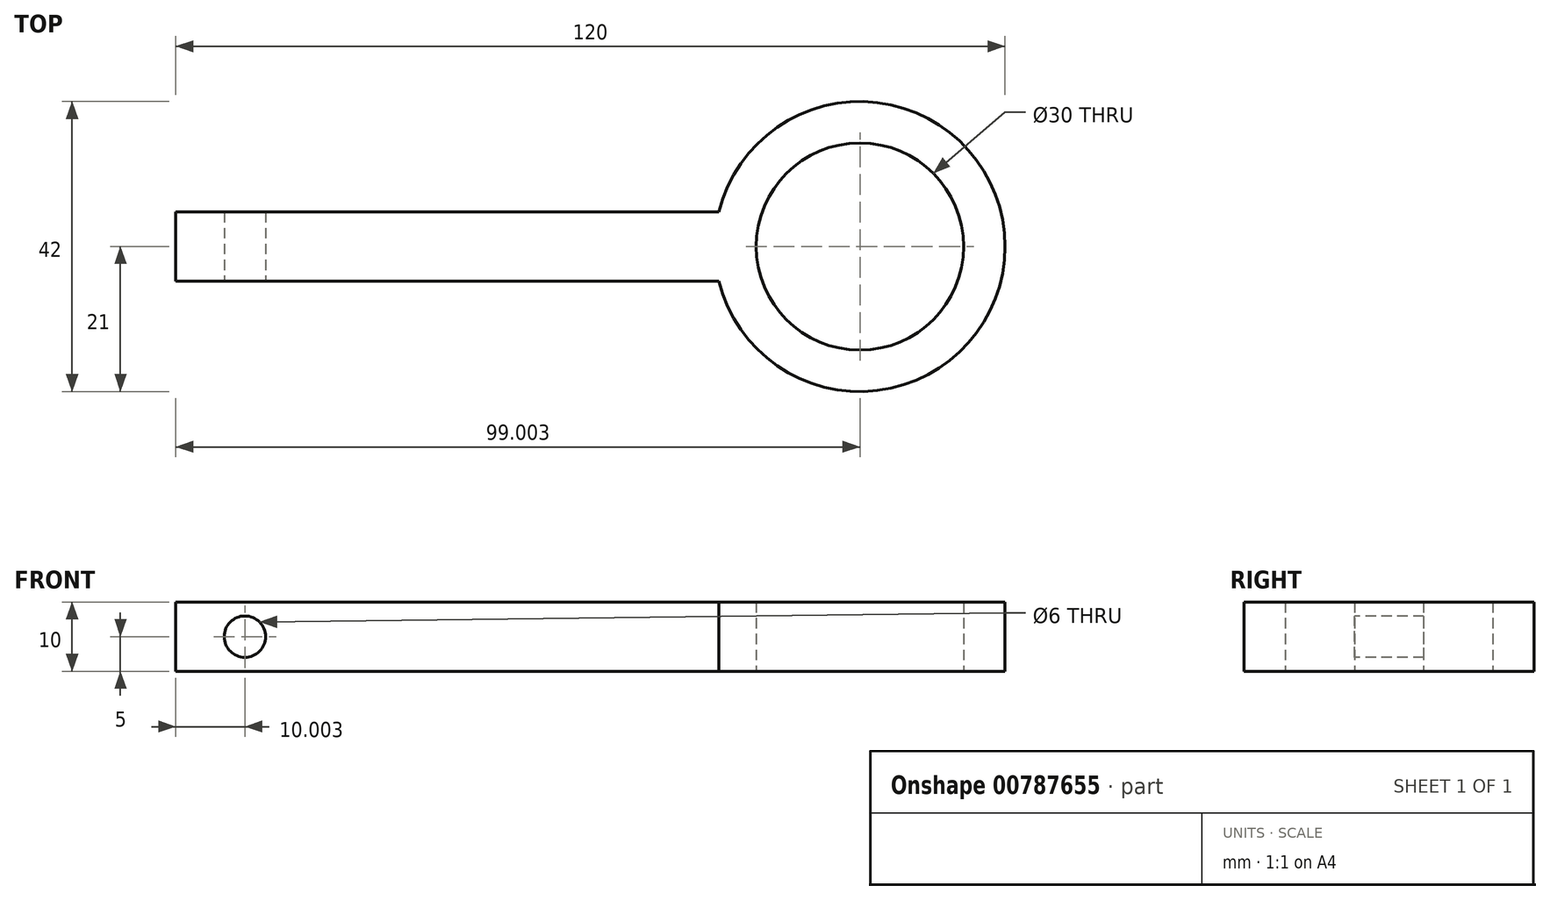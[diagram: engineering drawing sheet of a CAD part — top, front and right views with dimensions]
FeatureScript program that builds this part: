
annotation { "Feature Type Name" : "Feature", "Feature Type Description" : "" }
export const myFeature = defineFeature(function(context is Context, id is Id, definition is map)
    precondition{}
    {
        {
            var Q0;
            Q0=qCreatedBy(makeId("Top.planeOp"),FACE);
            var sketch = newSketch(context, id + "F0", { "sketchPlane" : qUnion([Q0])});
            skLineSegment(sketch, "E0.bottom", {"start": v(-74.3, 5) * mm, "end": v(4.3, 5) * mm});
            skLineSegment(sketch, "E0.top", {"start": v(-74.3, -5) * mm, "end": v(4.3, -5) * mm});
            skLineSegment(sketch, "E0.left", {"start": v(-74.3, 5) * mm, "end": v(-74.3, -5) * mm});
            skArc(sketch, "E1", {"start": v(4.3, -5) * mm, "mid": v(45.7, 0) * mm, "end": v(4.3, 5) * mm});
            skCircle(sketch, "E2", {"center": v(24.7, 0) * mm, "radius": 15 * mm});
            skPoint(sketch, "E3.start.orphan", {"position": v(-50, 0) * mm});
            skSolve(sketch);
        }
        {
            var Q0;
            {var subQ1=sQuery(id+"F0.wireOp",EDGE,"E0.left");Q0=makeQuery(id+"F0.imprint","IMPRINT",FACE,{"disambiguationData":[TD([[makeQuery(id+"F0.imprint","IMPRINT",EDGE,{"derivedFrom":subQ1}),1.0]])]});}
            extrude(context, id + "F1", {"entities" : qUnion([Q0]), "depth" : 10 * mm, "offsetDistance" : 25 * mm});
        }
        {
            var Q0;
            Q0=makeQuery(id+"F1.opExtrude","SWEPT_FACE",FACE,{"disambiguationData":[OSD([sQuery(id+"F0.wireOp",EDGE,"E0.top")])]});
            var sketch = newSketch(context, id + "F2", { "sketchPlane" : qUnion([Q0])});
            skCircle(sketch, "E4", {"center": v(-64.3, 5) * mm, "radius": 3 * mm});
            skSolve(sketch);
        }
        {
            var Q0;
            Q0 = qSketchRegion(id + "F2", true);
            extrude(context, id + "F3", {"entities" : qUnion([Q0]), "operationType" : NewBodyOperationType.REMOVE, "oppositeDirection" : true, "depth" : 25 * mm, "offsetDistance" : 25 * mm});
        }
    });
